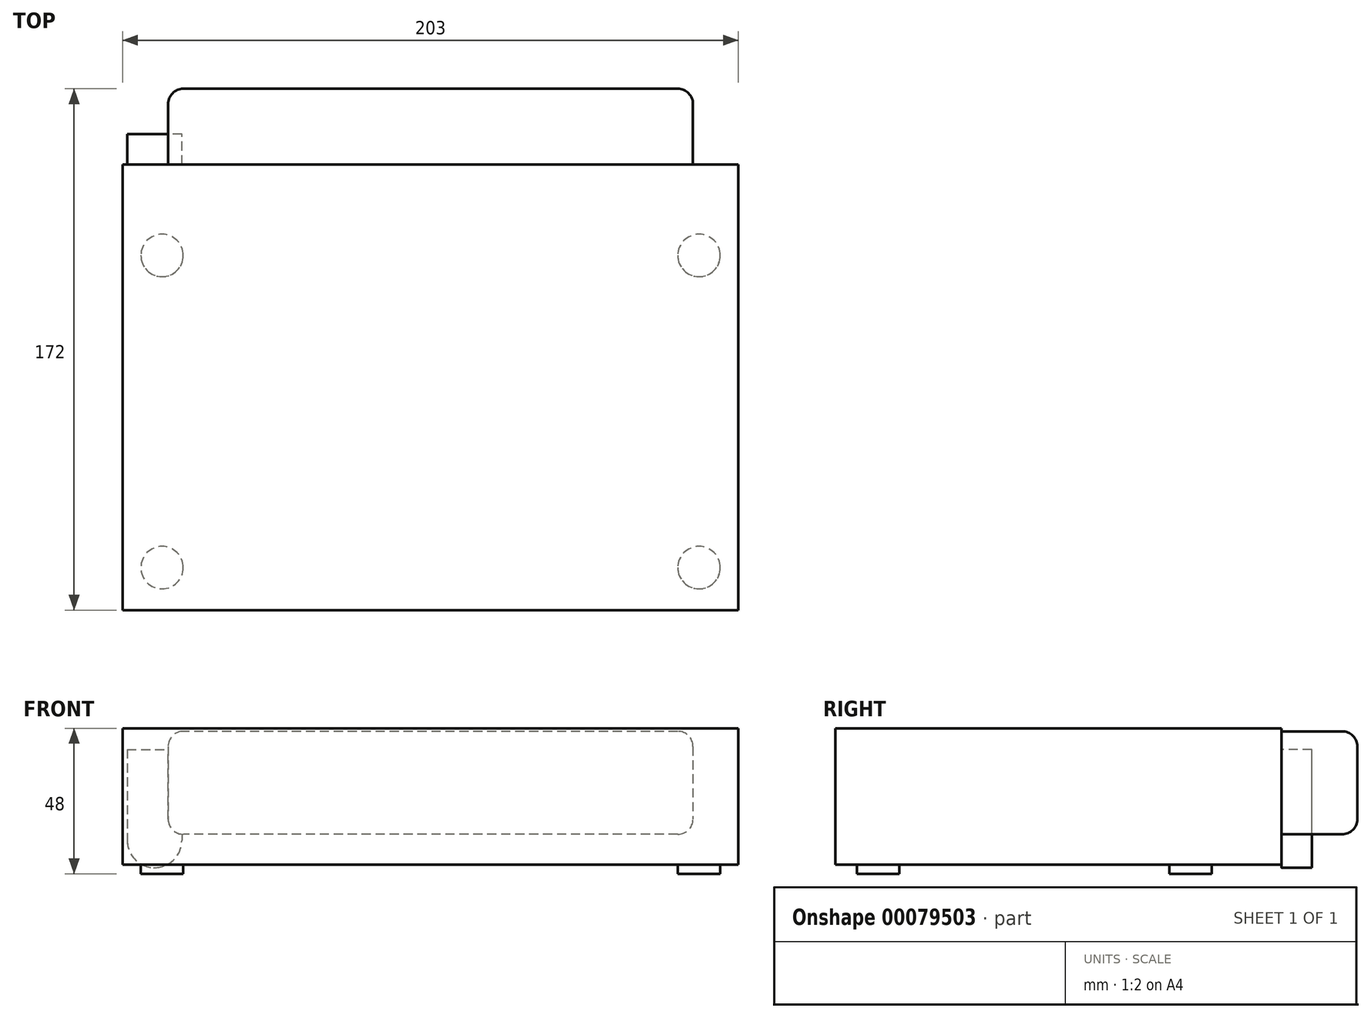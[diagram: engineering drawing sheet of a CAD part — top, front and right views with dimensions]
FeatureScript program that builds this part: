
annotation { "Feature Type Name" : "Feature", "Feature Type Description" : "" }
export const myFeature = defineFeature(function(context is Context, id is Id, definition is map)
    precondition{}
    {
        {
            var Q0;
            Q0=qCreatedBy(makeId("Top.planeOp"),FACE);
            var sketch = newSketch(context, id + "F0", { "sketchPlane" : qUnion([Q0])});
            skLineSegment(sketch, "E0.bottom", {"start": v(-101.5, 147) * mm, "end": v(101.5, 147) * mm});
            skLineSegment(sketch, "E0.top", {"start": v(-101.5, 0) * mm, "end": v(101.5, 0) * mm});
            skLineSegment(sketch, "E0.left", {"start": v(-101.5, 147) * mm, "end": v(-101.5, 0) * mm});
            skLineSegment(sketch, "E0.right", {"start": v(101.5, 147) * mm, "end": v(101.5, 0) * mm});
            skSolve(sketch);
        }
        {
            var Q0;
            Q0 = qSketchRegion(id + "F0", true);
            extrude(context, id + "F1", {"entities" : qUnion([Q0]), "depth" : 45 * mm});
        }
        {
            var Q0;
            Q0=makeQuery(id+"F1.opExtrude","CAP_FACE",FACE,{"disambiguationData":[OSD([sQuery(id+"F0.wireOp",EDGE,"E0.bottom"),sQuery(id+"F0.wireOp",EDGE,"E0.top"),sQuery(id+"F0.wireOp",EDGE,"E0.left"),sQuery(id+"F0.wireOp",EDGE,"E0.right")])],"isStart":true});
            var sketch = newSketch(context, id + "F2", { "sketchPlane" : qUnion([Q0])});
            skCircle(sketch, "E1", {"center": v(-88.5, -14) * mm, "radius": 7 * mm});
            skCircle(sketch, "E2", {"center": v(-88.5, -117) * mm, "radius": 7 * mm});
            skCircle(sketch, "E3.MirrorC", {"center": v(88.5, -14) * mm, "radius": 7 * mm});
            skCircle(sketch, "E4.MirrorC", {"center": v(88.5, -117) * mm, "radius": 7 * mm});
            skSolve(sketch);
        }
        {
            var Q0;
            Q0 = qSketchRegion(id + "F2", true);
            extrude(context, id + "F3", {"entities" : qUnion([Q0]), "operationType" : NewBodyOperationType.ADD, "depth" : 3 * mm});
        }
        {
            var Q0;
            Q0=makeQuery(id+"F1.opExtrude","SWEPT_FACE",FACE,{"disambiguationData":[OSD([sQuery(id+"F0.wireOp",EDGE,"E0.bottom")])]});
            var sketch = newSketch(context, id + "F4", { "sketchPlane" : qUnion([Q0])});
            skCircle(sketch, "E5", {"center": v(91, 8) * mm, "radius": 2 * mm, "construction": true});
            skCircle(sketch, "E6", {"center": v(91, 8) * mm, "radius": 9 * mm});
            skSolve(sketch);
        }
        {
            var Q0;
            Q0 = qSketchRegion(id + "F4", true);
            extrude(context, id + "F5", {"entities" : qUnion([Q0]), "operationType" : NewBodyOperationType.ADD, "depth" : 10 * mm});
        }
        {
            var Q0;
            Q0=makeQuery(id+"F1.opExtrude","SWEPT_FACE",FACE,{"disambiguationData":[OSD([sQuery(id+"F0.wireOp",EDGE,"E0.bottom")])]});
            var sketch = newSketch(context, id + "F6", { "sketchPlane" : qUnion([Q0])});
            skLineSegment(sketch, "E7.bottom", {"start": v(-86.5, 44) * mm, "end": v(86.5, 44) * mm});
            skLineSegment(sketch, "E7.top", {"start": v(-86.5, 10) * mm, "end": v(86.5, 10) * mm});
            skLineSegment(sketch, "E7.left", {"start": v(-86.5, 44) * mm, "end": v(-86.5, 10) * mm});
            skLineSegment(sketch, "E7.right", {"start": v(86.5, 44) * mm, "end": v(86.5, 10) * mm});
            skSolve(sketch);
        }
        {
            var Q0;
            Q0 = qSketchRegion(id + "F6", true);
            extrude(context, id + "F7", {"entities" : qUnion([Q0]), "operationType" : NewBodyOperationType.ADD, "depth" : 25 * mm});
        }
        {
            var Q0;
            Q0=makeQuery(id+"F7.opExtrude","CAP_FACE",FACE,{"disambiguationData":[OSD([sQuery(id+"F6.wireOp",EDGE,"E7.bottom"),sQuery(id+"F6.wireOp",EDGE,"E7.top"),sQuery(id+"F6.wireOp",EDGE,"E7.left"),sQuery(id+"F6.wireOp",EDGE,"E7.right")])],"isStart":false});
            var Q1;
            Q1=makeQuery(id+"F7.opExtrude","SWEPT_EDGE",EDGE,{"disambiguationData":[OSD([sQuery(id+"F6.wireOp",EDGE,"E7.bottom"),sQuery(id+"F6.wireOp",EDGE,"E7.left")])]});
            var Q2;
            Q2=makeQuery(id+"F7.opExtrude","SWEPT_EDGE",EDGE,{"disambiguationData":[OSD([sQuery(id+"F6.wireOp",EDGE,"E7.top"),sQuery(id+"F6.wireOp",EDGE,"E7.left")])]});
            var Q3;
            Q3=makeQuery(id+"F7.opExtrude","SWEPT_EDGE",EDGE,{"disambiguationData":[OSD([sQuery(id+"F6.wireOp",EDGE,"E7.bottom"),sQuery(id+"F6.wireOp",EDGE,"E7.right")])]});
            var Q4;
            Q4=makeQuery(id+"F7.opExtrude","SWEPT_EDGE",EDGE,{"disambiguationData":[OSD([sQuery(id+"F6.wireOp",EDGE,"E7.top"),sQuery(id+"F6.wireOp",EDGE,"E7.right")])]});
            fillet(context, id + "F8", {"entities" : qUnion([Q0, Q1, Q2, Q3, Q4]), "radius" : 5 * mm, "tangentPropagation" : true, "allowEdgeOverflow" : false});
        }
        {
            var Q0;
            Q0=makeQuery(id+"F5.opExtrude","CAP_FACE",FACE,{"disambiguationData":[OSD([sQuery(id+"F4.wireOp",EDGE,"E6")])],"isStart":false});
            var sketch = newSketch(context, id + "F9", { "sketchPlane" : qUnion([Q0])});
            skArc(sketch, "E8.0", {"start": v(82.24, 10.05) * mm, "mid": v(98.23, 2.63) * mm, "end": v(86.5, 15.8) * mm, "construction": true});
            skLineSegment(sketch, "E9.bottom", {"start": v(82, 8) * mm, "end": v(100, 8) * mm});
            skLineSegment(sketch, "E9.top", {"start": v(82, 38) * mm, "end": v(100, 38) * mm});
            skLineSegment(sketch, "E9.left", {"start": v(82, 8) * mm, "end": v(82, 38) * mm});
            skLineSegment(sketch, "E9.right", {"start": v(100, 8) * mm, "end": v(100, 38) * mm});
            skSolve(sketch);
        }
        {
            var Q0;
            Q0 = qSketchRegion(id + "F9", true);
            var Q1;
            Q1=makeQuery(id+"F1.opExtrude","SWEPT_FACE",FACE,{"disambiguationData":[OSD([sQuery(id+"F0.wireOp",EDGE,"E0.bottom")])]});
            extrude(context, id + "F10", {"entities" : qUnion([Q0]), "operationType" : NewBodyOperationType.ADD, "endBound" : BoundingType.UP_TO_SURFACE, "oppositeDirection" : true, "endBoundEntityFace" : qUnion([Q1]), "depth" : 25 * mm});
        }
    });
